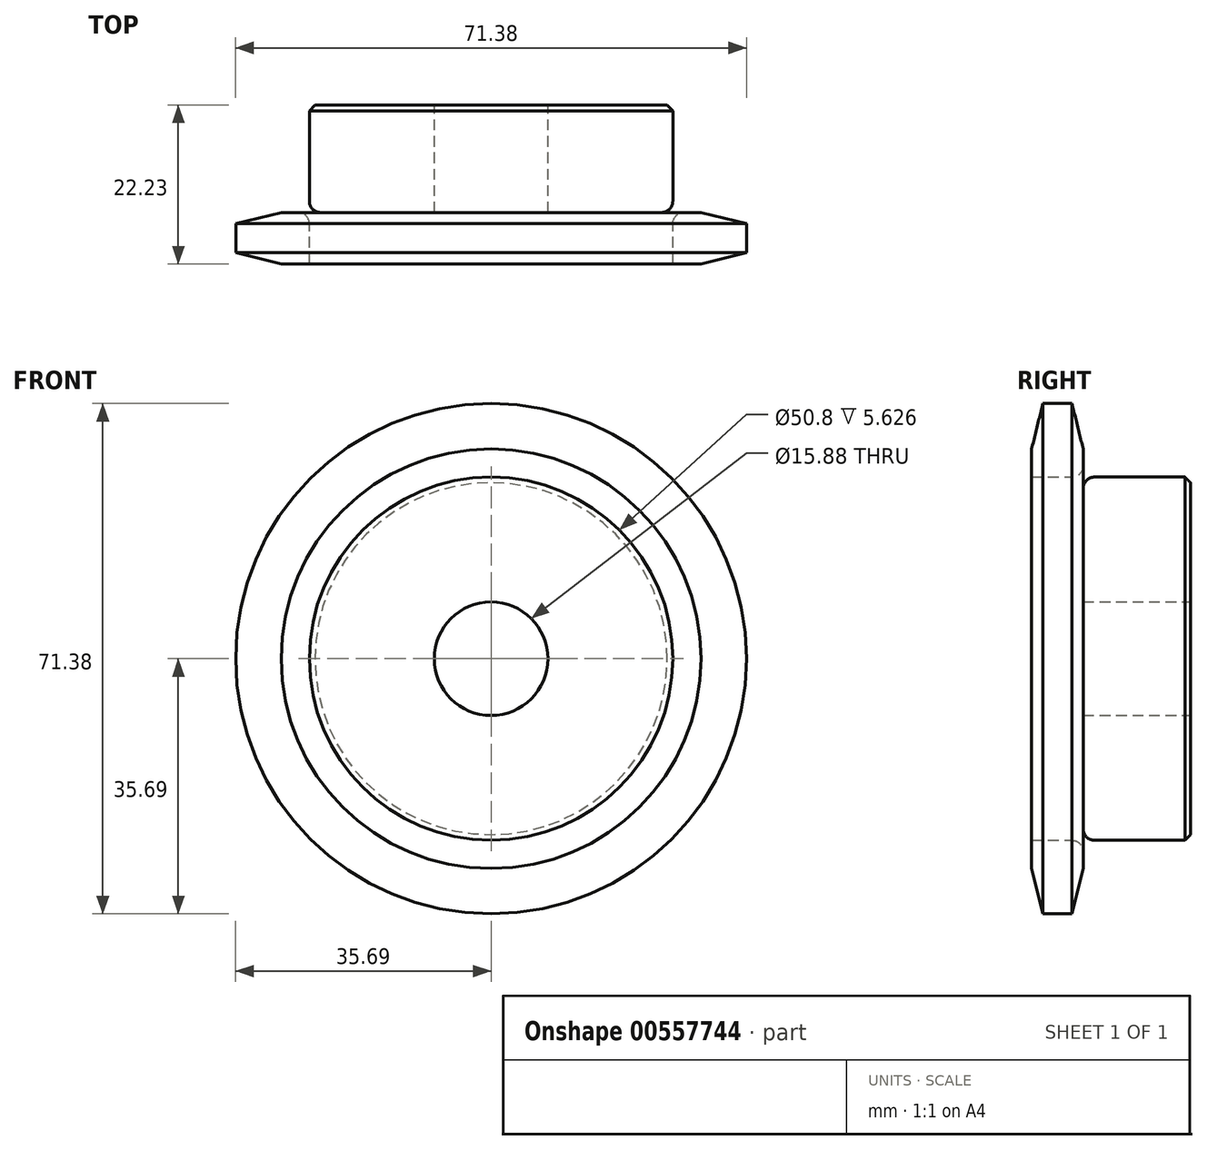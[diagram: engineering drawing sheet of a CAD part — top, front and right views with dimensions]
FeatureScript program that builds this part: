
annotation { "Feature Type Name" : "Feature", "Feature Type Description" : "" }
export const myFeature = defineFeature(function(context is Context, id is Id, definition is map)
    precondition{}
    {
        {
            var Q0;
            Q0=qCreatedBy(makeId("Right.planeOp"),FACE);
            var sketch = newSketch(context, id + "F0", { "sketchPlane" : qUnion([Q0])});
            skLineSegment(sketch, "E0", {"start": v(22.23, 0) * mm, "end": v(0, 0) * mm});
            skLineSegment(sketch, "E1.bottom", {"start": v(0, 7.94) * mm, "end": v(7.21, 7.94) * mm});
            skLineSegment(sketch, "E1.top", {"start": v(0, 35.69) * mm, "end": v(7.21, 35.69) * mm});
            skLineSegment(sketch, "E1.left", {"start": v(0, 7.94) * mm, "end": v(0, 35.69) * mm});
            skLineSegment(sketch, "E1.right", {"start": v(7.21, 7.94) * mm, "end": v(7.21, 35.69) * mm});
            skLineSegment(sketch, "E2.bottom", {"start": v(0, 7.94) * mm, "end": v(22.22, 7.94) * mm});
            skLineSegment(sketch, "E2.top", {"start": v(0, 25.4) * mm, "end": v(22.22, 25.4) * mm});
            skLineSegment(sketch, "E2.left", {"start": v(0, 7.94) * mm, "end": v(0, 25.4) * mm});
            skLineSegment(sketch, "E2.right", {"start": v(22.23, 7.94) * mm, "end": v(22.23, 25.4) * mm});
            skLineSegment(sketch, "E3.MirrorCS", {"start": v(0, -7.94) * mm, "end": v(7.21, -7.94) * mm});
            skLineSegment(sketch, "E4.MirrorCS", {"start": v(22.23, -7.94) * mm, "end": v(22.23, -25.4) * mm});
            skLineSegment(sketch, "E5.MirrorCS", {"start": v(0, -7.94) * mm, "end": v(0, -25.4) * mm});
            skLineSegment(sketch, "E6.MirrorCS", {"start": v(0, -25.4) * mm, "end": v(22.23, -25.4) * mm});
            skLineSegment(sketch, "E7.MirrorCS", {"start": v(0, -35.69) * mm, "end": v(7.21, -35.69) * mm});
            skLineSegment(sketch, "E8.MirrorCS", {"start": v(0, -7.94) * mm, "end": v(0, -35.69) * mm});
            skLineSegment(sketch, "E9.MirrorCS", {"start": v(7.21, -7.94) * mm, "end": v(7.21, -35.69) * mm});
            skLineSegment(sketch, "E10.MirrorCS", {"start": v(0, -7.94) * mm, "end": v(22.22, -7.94) * mm});
            skSolve(sketch);
        }
        {
            var Q0;
            {var subQ0=sQuery(id+"F0.wireOp",EDGE,"E1.top");Q0=makeQuery(id+"F0.imprint","IMPRINT",FACE,{"disambiguationData":[TD([[makeQuery(id+"F0.imprint","IMPRINT",EDGE,{"derivedFrom":subQ0}),-1.0]])]});}
            var Q1;
            {var subQ5=sQuery(id+"F0.wireOp",EDGE,"E2.left");Q1=makeQuery(id+"F0.imprint","IMPRINT",FACE,{"disambiguationData":[TD([[makeQuery(id+"F0.imprint","IMPRINT",EDGE,{"derivedFrom":subQ5}),-1.0]])]});}
            var Q2;
            {var subQ5=sQuery(id+"F0.wireOp",EDGE,"E2.right");Q2=makeQuery(id+"F0.imprint","IMPRINT",FACE,{"disambiguationData":[TD([[makeQuery(id+"F0.imprint","IMPRINT",EDGE,{"derivedFrom":subQ5}),1.0]])]});}
            var Q3;
            Q3=sQuery(id+"F0.wireOp",EDGE,"E0");
            revolve(context, id + "F1", {"entities" : qUnion([Q0, Q1, Q2]), "axis" : qUnion([Q3]), "revolveType" : RevolveType.FULL});
        }
        {
            var Q0;
            Q0=makeQuery(id+"F1.opRevolve","SWEPT_EDGE",EDGE,{"disambiguationData":[OSD([sQuery(id+"F0.wireOp",EDGE,"E1.right"),sQuery(id+"F0.wireOp",EDGE,"E2.top")])]});
            fillet(context, id + "F2", {"entities" : qUnion([Q0]), "radius" : 1.59 * mm, "tangentPropagation" : true, "allowEdgeOverflow" : false});
        }
        {
            var Q0;
            Q0=makeQuery(id+"F1.opRevolve","SWEPT_EDGE",EDGE,{"disambiguationData":[OSD([sQuery(id+"F0.wireOp",EDGE,"E2.top"),sQuery(id+"F0.wireOp",EDGE,"E2.right")])]});
            chamfer(context, id + "F3", {"entities" : qUnion([Q0]), "width" : 0.8 * mm, "tangentPropagation" : true});
        }
        {
            var Q0;
            Q0=makeQuery(id+"F1.opRevolve","SWEPT_EDGE",EDGE,{"disambiguationData":[OSD([sQuery(id+"F0.wireOp",EDGE,"E1.top"),sQuery(id+"F0.wireOp",EDGE,"E1.right")])]});
            var Q1;
            Q1=makeQuery(id+"F1.opRevolve","SWEPT_EDGE",EDGE,{"disambiguationData":[OSD([sQuery(id+"F0.wireOp",EDGE,"E1.top"),sQuery(id+"F0.wireOp",EDGE,"E1.left")])]});
            chamfer(context, id + "F4", {"entities" : qUnion([Q0, Q1]), "chamferType" : ChamferType.TWO_OFFSETS, "width1" : 6.35 * mm, "oppositeDirection" : false, "width2" : 1.57 * mm, "tangentPropagation" : true});
        }
    });
